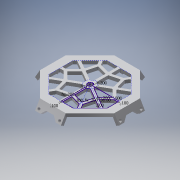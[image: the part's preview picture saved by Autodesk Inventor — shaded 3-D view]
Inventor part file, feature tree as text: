
AUTODESK INVENTOR PART (.ipt)
format: ipt  version: 2019 (Build 230136000, 136)  size: 567,296 bytes
history: native  units: in
note: dims shown in document units (in); Inventor stores cm internally (conversion verified against a paired STEP export)
features: extrude x5, sketch x5, pattern_circular x2, mirror x2, fillet x2, projected_geometry x2, hole x1
ambient origin geometry x8: Origin, YZ Plane, XZ Plane, XY Plane, X Axis, Y Axis, Z Axis, Center Point
bodies: Solid1 (feature_tree)
feature tree (19):
  extrude  "Extrusion1"  Depth=2.0in
  pattern_circular  "Circular Pattern1"  [2 undecoded]
  extrude  "Extrusion2"  Depth=0.25in
  sketch  "Sketch3"  dims[d3=30.0deg]
  extrude  "Extrusion3"  Depth=2.0in TaperAngle=0.0deg
  hole  "Hole1"  [1 undecoded]
  extrude  "Extrusion4"  Depth=0.25in
  pattern_circular  "Circular Pattern2"  [2 undecoded]
  extrude  "Extrusion6"  TaperAngle=45.0deg  [1 undecoded]
  mirror  "Mirror1"
  mirror  "Mirror2"
  fillet  "Fillet2"  Radius=0.4in
  fillet  "Fillet3"  Radius=0.31in
  sketch  "Sketch1"  dims[d0=2.0in d1=1.0in]
  sketch  "Sketch2"  dims[d2=2.5in]
  projected_geometry  "Projected Loop1"
  projected_geometry  "Projected Loop2"
  sketch  "Sketch5"  dims[d4=4.5in]
  sketch  "Sketch6"  dims[d5=0.6in d6=4.2in d7=0.25in d8=2.0in d9=0.0in d10=1.5748in d11=360.0deg d14=0.25in d17=2.5in d18=0.0in d19=45.0deg d20=0.4in d21=0.31in d22=2.5in d23=0.0in d24=0.2in d25=0.2in d26=0.2in d27=0.203in d28=0.75in d29=0.375in d30=0.25in d31=0.5635in d32=1.0in d33=0.8108in d34=0.25in d35=0.45in d36=0.2in d37=0.0in d38=1.5748in d39=360.0deg d41=0.377in d42=0.1in d43=0.2in d45=30.0deg d46=0.2in d48=0.2in d49=0.1in d50=0.2in d51=0.2in d52=0.2in d59=0.2in d60=0.0in d61=0.5in d64=2.25in d65=2.25in d67=0.0625in d68=0.0625in d69=0.0625in]
note: 6 required parameter values undecoded (feature->parameter linkage not recoverable at this tier; creation-order binding heuristic only, values carry confidence <= 0.55)
